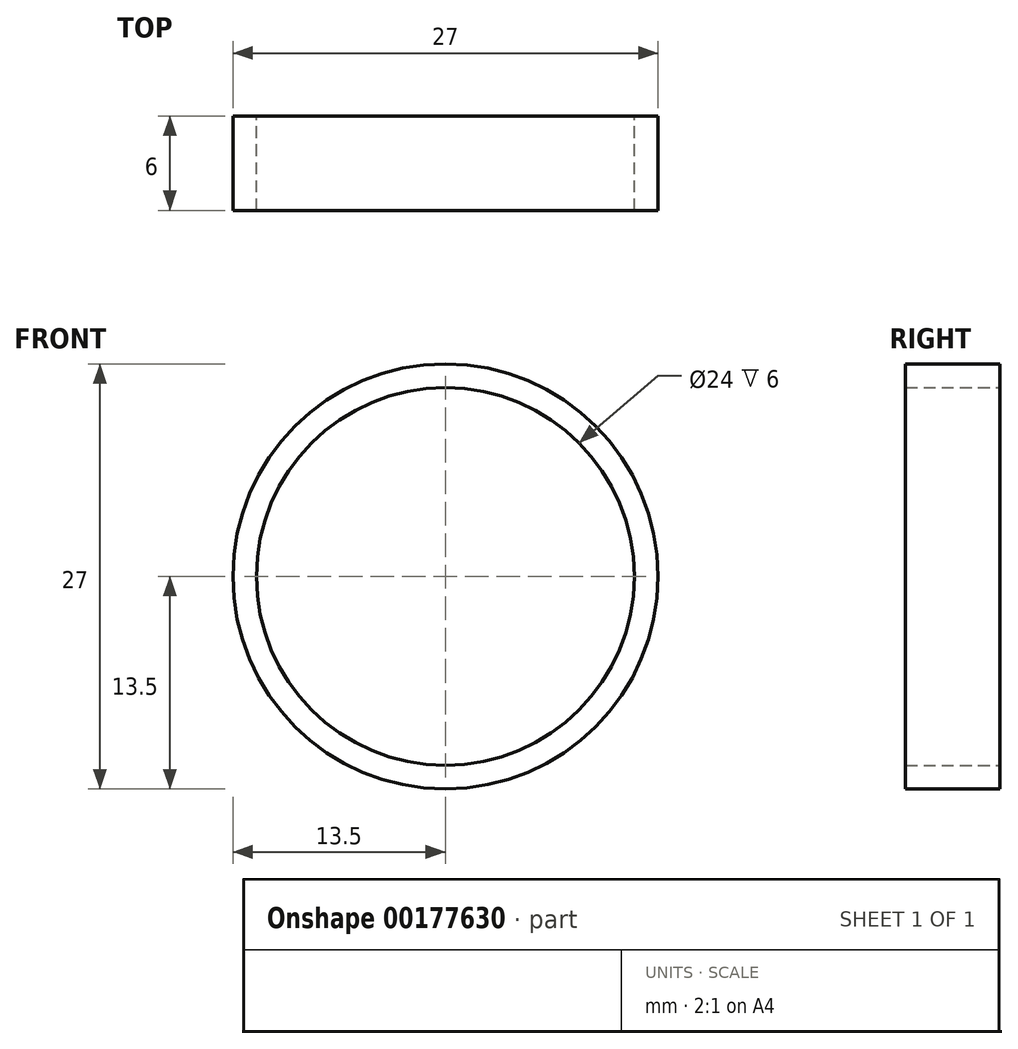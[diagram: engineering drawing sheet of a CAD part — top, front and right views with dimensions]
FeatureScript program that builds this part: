
annotation { "Feature Type Name" : "Feature", "Feature Type Description" : "" }
export const myFeature = defineFeature(function(context is Context, id is Id, definition is map)
    precondition{}
    {
        {
            var Q0;
            Q0=qCreatedBy(makeId("Front.planeOp"),FACE);
            var sketch = newSketch(context, id + "F0", { "sketchPlane" : qUnion([Q0])});
            skCircle(sketch, "E0", {"center": v(0, 0) * mm, "radius": 13.5 * mm});
            skCircle(sketch, "E1", {"center": v(0, 0) * mm, "radius": 12 * mm});
            skSolve(sketch);
        }
        {
            var Q0;
            Q0 = qSketchRegion(id + "F0", true);
            extrude(context, id + "F1", {"entities" : qUnion([Q0]), "depth" : 6 * mm});
        }
    });
